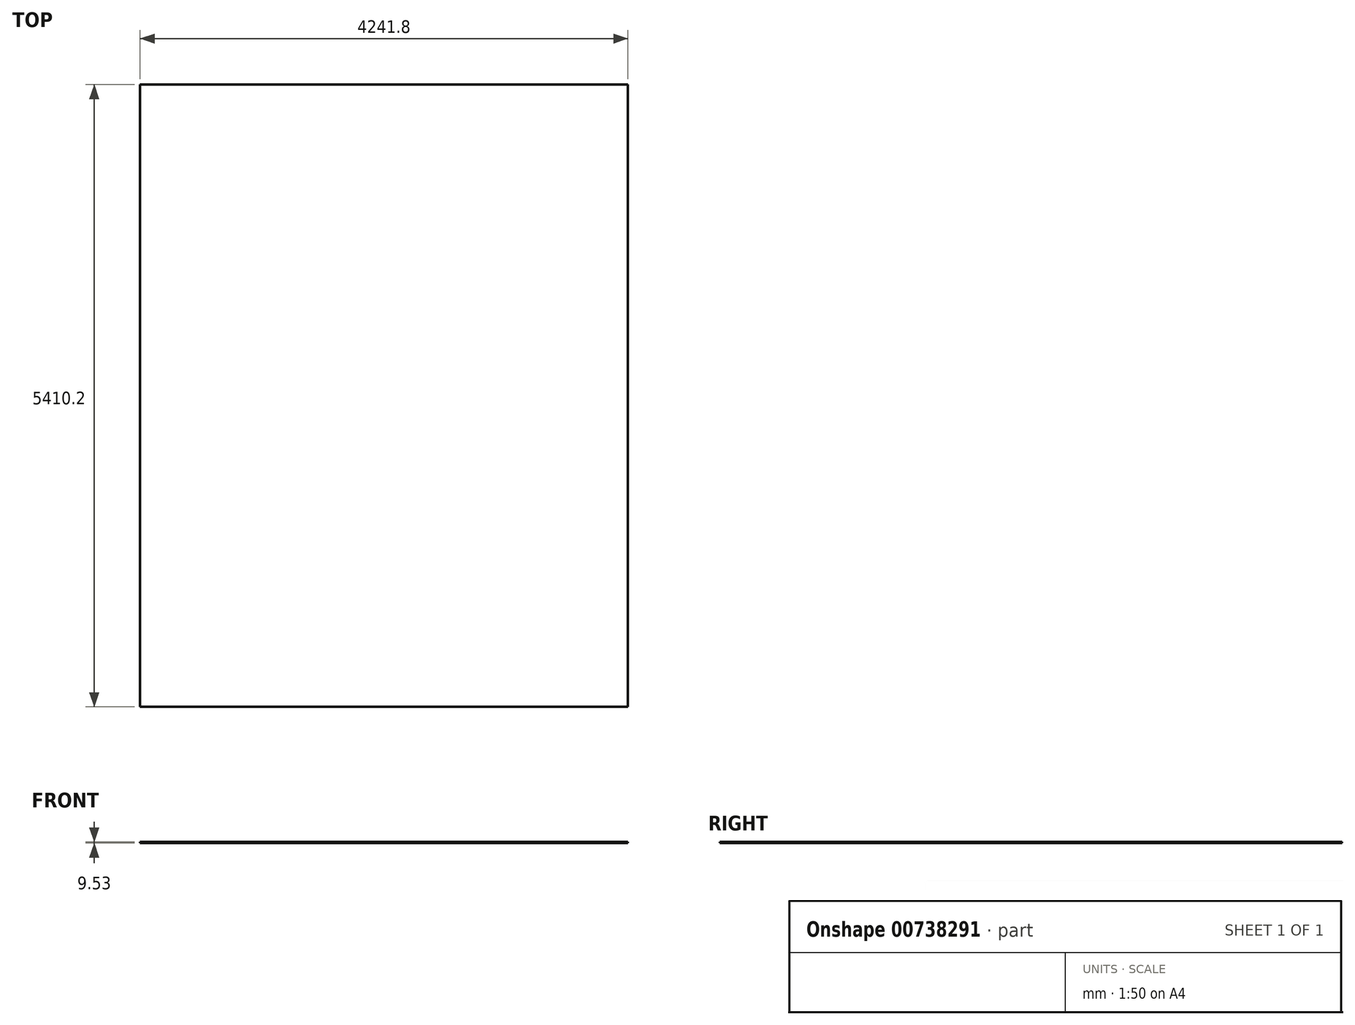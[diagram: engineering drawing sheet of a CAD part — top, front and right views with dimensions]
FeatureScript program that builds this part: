
annotation { "Feature Type Name" : "Feature", "Feature Type Description" : "" }
export const myFeature = defineFeature(function(context is Context, id is Id, definition is map)
    precondition{}
    {
        {
            var Q0;
            Q0=qCreatedBy(makeId("Top.planeOp"),FACE);
            var sketch = newSketch(context, id + "F0", { "sketchPlane" : qUnion([Q0])});
            skLineSegment(sketch, "E0.bottom", {"start": v(2120.9, -2705.1) * mm, "end": v(-2120.9, -2705.1) * mm});
            skLineSegment(sketch, "E0.top", {"start": v(2120.9, 2705.1) * mm, "end": v(-2120.9, 2705.1) * mm});
            skLineSegment(sketch, "E0.left", {"start": v(2120.9, -2705.1) * mm, "end": v(2120.9, 2705.1) * mm});
            skLineSegment(sketch, "E0.right", {"start": v(-2120.9, -2705.1) * mm, "end": v(-2120.9, 2705.1) * mm});
            skPoint(sketch, "E0.middle", {"position": v(0, 0) * mm});
            skSolve(sketch);
        }
        {
            var Q0;
            Q0=makeQuery(id+"F0.imprint","IMPRINT",FACE,{"disambiguationData":[TD([[makeQuery(id+"F0.imprint","IMPRINT",EDGE,{"derivedFrom":sQuery(id+"F0.wireOp",EDGE,"E0.bottom")}),-1.0]])]});
            extrude(context, id + "F1", {"entities" : qUnion([Q0]), "oppositeDirection" : true, "depth" : 9.52 * mm, "offsetDistance" : 25.4 * mm});
        }
    });
